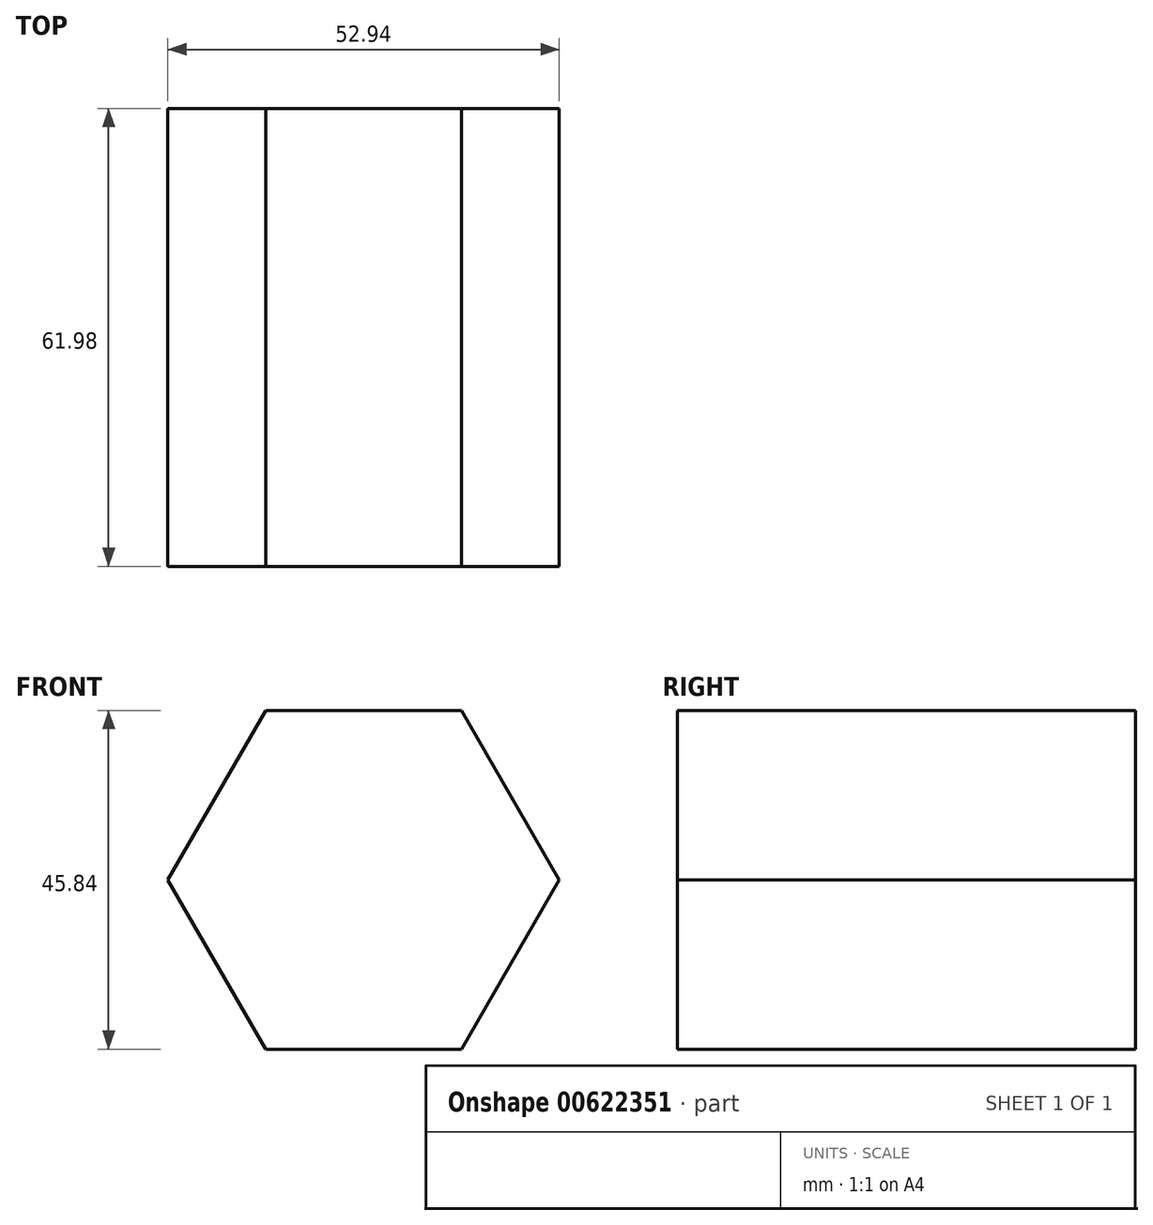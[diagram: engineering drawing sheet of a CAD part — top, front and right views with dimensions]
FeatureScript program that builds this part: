
annotation { "Feature Type Name" : "Feature", "Feature Type Description" : "" }
export const myFeature = defineFeature(function(context is Context, id is Id, definition is map)
    precondition{}
    {
        {
            var Q0;
            Q0=qCreatedBy(makeId("Front.planeOp"),FACE);
            var sketch = newSketch(context, id + "F0", { "sketchPlane" : qUnion([Q0])});
            skCircle(sketch, "E0.cCircle", {"center": v(0, 0) * mm, "radius": 22.92 * mm, "construction": true});
            skLineSegment(sketch, "E0.0", {"start": v(-13.23, 22.92) * mm, "end": v(13.23, 22.92) * mm});
            skLineSegment(sketch, "E0.1", {"start": v(13.23, 22.92) * mm, "end": v(26.47, 0) * mm});
            skLineSegment(sketch, "E0.2", {"start": v(26.47, 0) * mm, "end": v(13.23, -22.92) * mm});
            skLineSegment(sketch, "E0.3", {"start": v(13.23, -22.92) * mm, "end": v(-13.23, -22.92) * mm});
            skLineSegment(sketch, "E0.4", {"start": v(-13.23, -22.92) * mm, "end": v(-26.47, 0) * mm});
            skLineSegment(sketch, "E0.5", {"start": v(-26.47, 0) * mm, "end": v(-13.23, 22.92) * mm});
            skPoint(sketch, "E0.0.midPoint", {"position": v(0, 22.92) * mm});
            skSolve(sketch);
        }
        {
            var Q0;
            Q0=makeQuery(id+"F0.imprint","IMPRINT",FACE,{"disambiguationData":[TD([[makeQuery(id+"F0.imprint","IMPRINT",EDGE,{"derivedFrom":sQuery(id+"F0.wireOp",EDGE,"E0.0")}),-1.0]])]});
            extrude(context, id + "F1", {"entities" : qUnion([Q0]), "depth" : 61.98 * mm, "offsetDistance" : 25.4 * mm});
        }
    });
